FCSTD DOCUMENT  (FreeCAD 0.21R33668 +26 (Git))
Label: Tuto1-000
License: All rights reserved
LicenseURL: http://en.wikipedia.org/wiki/All_rights_reserved
objects: App::DocumentObjectGroup×3, Sketcher::SketchObject×1, PartDesign::Body×1, PartDesign::CoordinateSystem×1, App::FeaturePython×1, App::Link×1, App::Part×1
note: 3 computed .brp shape members not serialized (recipe doc carries the construction recipe); baked Part::Feature solids carry a one-line shape summary decoded from their .brp

FEATURE [Sketcher::SketchObject] Sketch
  FullyConstrained = true
  MapMode = 5
  Placement = pos=(0,0,0) rot=(0.57735,0.57735,0.57735;2.0944rad)
  Support = -> [YZ_Plane001]
  expr: Constraints[11] = Variables.rotation_bielle1
  sketch-geometry (3):
    g0: LineSegment StartX=0 StartY=50 StartZ=0 EndX=95.4594 EndY=145.459 EndZ=0
    g1: LineSegment StartX=0 StartY=120 StartZ=0 EndX=95.4594 EndY=215.459 EndZ=0
    g2: LineSegment StartX=95.4594 StartY=245.459 StartZ=0 EndX=95.4594 EndY=115.459 EndZ=0
  constraints (12):
    c: PointOnObject(g0,g-2)
    c: PointOnObject(g1,g-2)
    c: PointOnObject(g1,g2)
    c: PointOnObject(g0,g2)
    c: DistanceY(g-1,g0) = 50
    c: DistanceY(g-1,g1) = 120
    c: Distance(g2,g1) = 30
    c: Distance(g0,g2) = 30
    c: Distance(g2,g2) = 130
    c: Distance(g1) = 135
    c: Distance(g0) = 135
    c: Angle(g-1,g1) = 0.785398
FEATURE [PartDesign::Body] Body  label="Corps"
  Group = -> [Sketch]
  Origin = -> Origin001
FEATURE [App::DocumentObjectGroup] Parts
  Group = -> [Body]
FEATURE [PartDesign::CoordinateSystem] LCS_Origin
  AttacherType = Attacher::AttachEngine3D
  MapMode = 2
  Support = -> [X_Axis]
FEATURE [App::DocumentObjectGroup] Constraints
FEATURE [App::FeaturePython] Variables  # WARN: FeaturePython — macro-defined, semantics opaque (R4)
  Type = App::PropertyContainer
  rotation_bielle1 = 45
FEATURE [App::DocumentObjectGroup] Configurations
FEATURE [App::Link] Corps  label="Corps001"
  LinkedObject = -> Body
FEATURE [App::Part] Assembly
  AssemblyType = Part::Link
  Group = -> [LCS_Origin,Constraints,Variables,Configurations,Corps]
  Origin = -> Origin
  Type = Assembly
